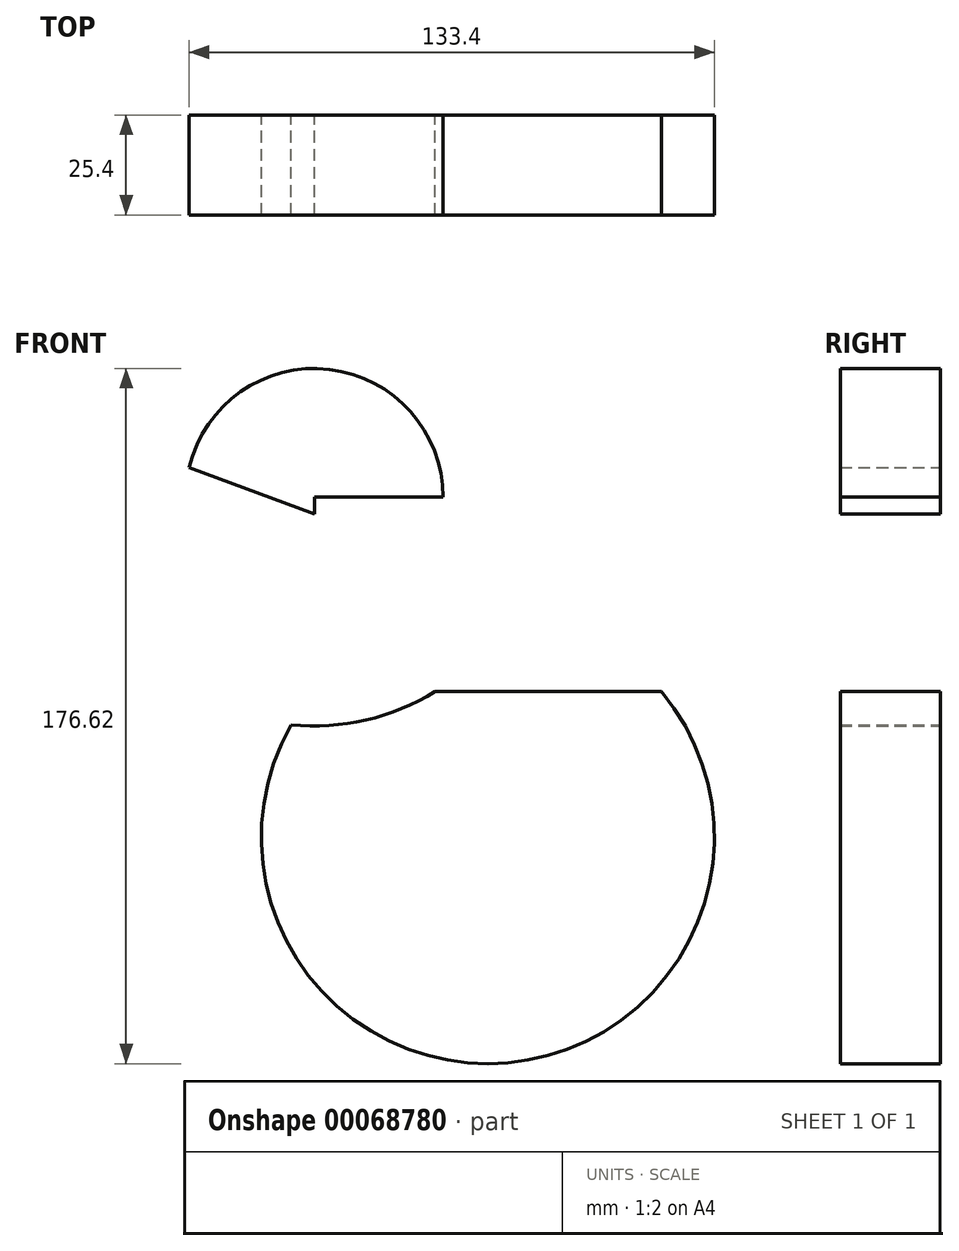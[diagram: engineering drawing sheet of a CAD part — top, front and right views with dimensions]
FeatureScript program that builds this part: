
annotation { "Feature Type Name" : "Feature", "Feature Type Description" : "" }
export const myFeature = defineFeature(function(context is Context, id is Id, definition is map)
    precondition{}
    {
        {
            var Q0;
            Q0=qCreatedBy(makeId("Front.planeOp"),FACE);
            var sketch = newSketch(context, id + "F0", { "sketchPlane" : qUnion([Q0])});
            skLineSegment(sketch, "E0", {"start": v(-43.87, -24.7) * mm, "end": v(-43.87, 24.7) * mm});
            skLineSegment(sketch, "E1", {"start": v(-43.87, -24.7) * mm, "end": v(44.25, -24.7) * mm});
            skLineSegment(sketch, "E2", {"start": v(44.25, -24.7) * mm, "end": v(44.25, 24.7) * mm});
            skLineSegment(sketch, "E3", {"start": v(-43.87, 24.7) * mm, "end": v(44.25, 24.7) * mm});
            skLineSegment(sketch, "E4", {"start": v(-43.87, 0) * mm, "end": v(44.25, 0) * mm, "construction": true});
            skLineSegment(sketch, "E5", {"start": v(-43.87, -24.7) * mm, "end": v(-122.2, 4.34) * mm});
            skLineSegment(sketch, "E6", {"start": v(-122.2, 4.34) * mm, "end": v(-122.2, 49.48) * mm});
            skLineSegment(sketch, "E7", {"start": v(-122.2, 49.48) * mm, "end": v(-43.87, 20.45) * mm});
            skLineSegment(sketch, "E8.bottom", {"start": v(58.86, -57.73) * mm, "end": v(76.81, -57.73) * mm});
            skLineSegment(sketch, "E8.top", {"start": v(58.86, -32.6) * mm, "end": v(76.81, -32.6) * mm});
            skLineSegment(sketch, "E8.left", {"start": v(58.86, -57.73) * mm, "end": v(58.86, -32.6) * mm});
            skLineSegment(sketch, "E8.right", {"start": v(76.81, -57.73) * mm, "end": v(76.81, -32.6) * mm});
            skCircle(sketch, "E9", {"center": v(44.25, 24.7) * mm, "radius": 22.41 * mm});
            skCircle(sketch, "E10", {"center": v(-43.87, 24.7) * mm, "radius": 58.13 * mm});
            skCircle(sketch, "E11.0", {"center": v(-43.87, 24.7) * mm, "radius": 32.68 * mm});
            skArc(sketch, "E12", {"start": v(-43.87, -24.7) * mm, "mid": v(0.19, -119.25) * mm, "end": v(44.25, -24.7) * mm});
            skArc(sketch, "E13", {"start": v(-132.97, 77.69) * mm, "mid": v(-86.1, 50.04) * mm, "end": v(-50.9, 91.54) * mm});
            skSolve(sketch);
        }
        {
            var Q0;
            {var subQ0=sQuery(id+"F0.wireOp",EDGE,"E12");var subQ3=sQuery(id+"F0.wireOp",EDGE,"E10");var subQ5=makeQuery(id+"F0.imprint","INTERSECT",VERTEX,{"derivedFrom":[subQ3,subQ0]});Q0=makeQuery(id+"F0.imprint","IMPRINT",FACE,{"disambiguationData":[TD([[makeQuery(id+"F0.imprint","IMPRINT",EDGE,{"disambiguationData":[TD([[subQ5,-1.0]])],"derivedFrom":subQ3}),-1.0]])]});}
            var Q1;
            {var subQ0=sQuery(id+"F0.wireOp",EDGE,"E3");var subQ1=sQuery(id+"F0.wireOp",EDGE,"E0");var subQ2=makeQuery(id+"F0.imprint","INTERSECT",VERTEX,{"derivedFrom":[subQ1,subQ0]});Q1=makeQuery(id+"F0.imprint","IMPRINT",FACE,{"disambiguationData":[TD([[makeQuery(id+"F0.imprint","IMPRINT",EDGE,{"disambiguationData":[TD([[subQ2,1.0]])],"derivedFrom":subQ1}),1.0]])]});}
            extrude(context, id + "F1", {"entities" : qUnion([Q0, Q1]), "depth" : 25.4 * mm});
        }
    });
